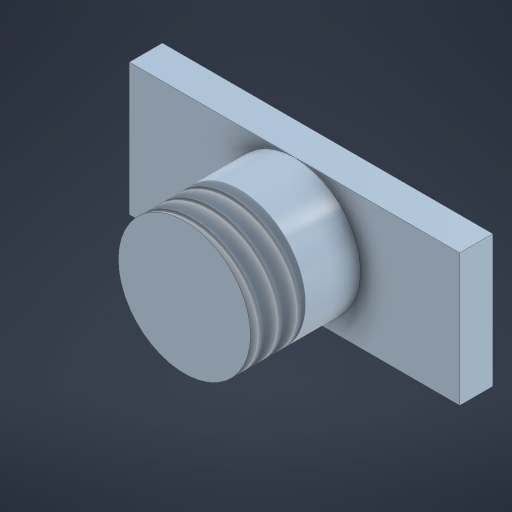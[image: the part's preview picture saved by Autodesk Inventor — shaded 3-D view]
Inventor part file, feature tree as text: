
AUTODESK INVENTOR PART (.ipt)
format: ipt  version: 2023 (Build 270158000, 158)  size: 214,528 bytes
history: native  units: mm
features: extrude x2, sketch x2, thread x1
ambient origin geometry x8: Origin, YZ Plane, XZ Plane, XY Plane, X Axis, Y Axis, Z Axis, Center Point
bodies: Solid1 (feature_tree)
feature tree (5):
  extrude  "Extrusion1"  Depth=12.0mm
  extrude  "Extrusion2"  Depth=12.0mm
  thread  "Thread2"  [1 undecoded]
  sketch  "Sketch1"  dims[d0=30.0mm d1=12.0mm]
  sketch  "Sketch2"  dims[d2=3.0mm d3=0.0mm d4=12.0mm d5=10.0mm d6=0.0mm d16=5.0mm d17=0.0mm d18=0.5mm d19=0.872665mm]
note: 1 required parameter value undecoded (feature->parameter linkage not recoverable at this tier; creation-order binding heuristic only, values carry confidence <= 0.55)
